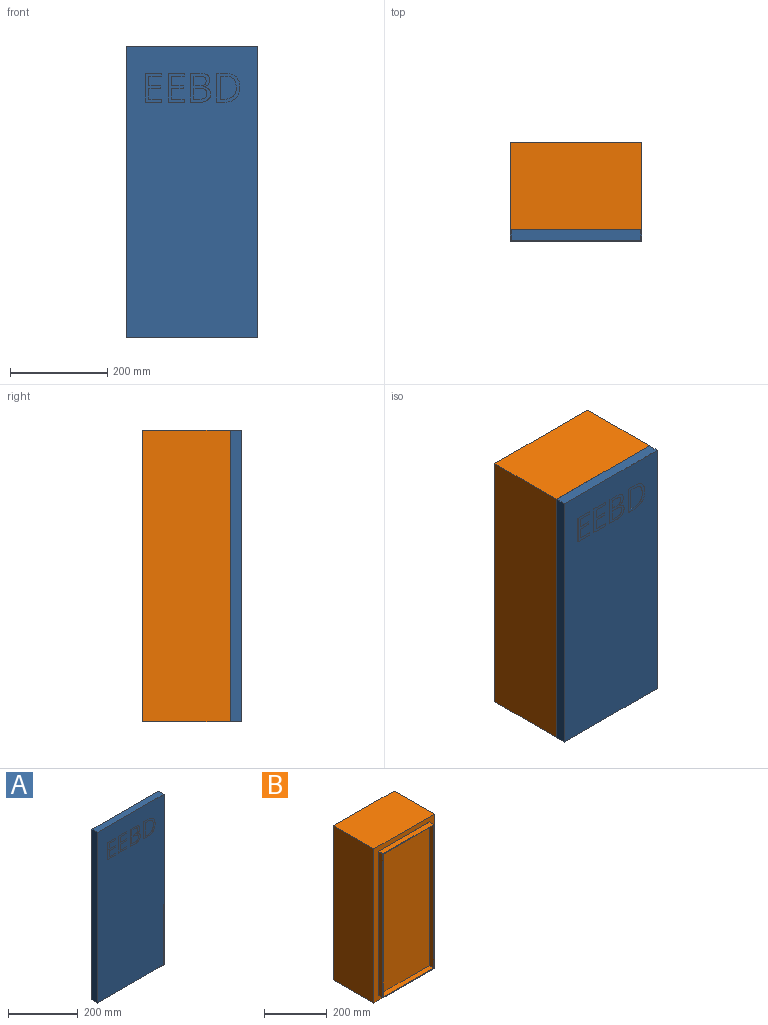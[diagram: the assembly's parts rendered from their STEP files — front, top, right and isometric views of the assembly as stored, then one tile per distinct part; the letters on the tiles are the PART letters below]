
ASSEMBLY  parts=2 mates=1
PART A: 81 faces, bbox 270x23.1x600 mm
  f0: plane 600x270mm, normal (0,-1,0), area 155520.7mm2, adj f1,f2,f3,f4,f11,f12,f13,f14
  f1: plane 600x23mm, normal (-1,0,0), area 13800mm2, adj f0,f2,f4,f5
  f2: plane 270x23mm, normal (0,0,-1), area 6210mm2, adj f0,f1,f3,f5
  f3: plane 600x23mm, normal (1,0,0), area 13800mm2, adj f0,f2,f4,f5
  f4: plane 270x23mm, normal (0,0,1), area 6210mm2, adj f0,f1,f3,f5
  f5: plane 600x270mm, normal (0,1,0), area 3464mm2, adj f1,f2,f3,f4,f6,f7,f8,f9
  f6: plane 596x21mm, normal (1,0,0), area 12516mm2, adj f5,f7,f9,f10
  f7: plane 266x21mm, normal (0,0,1), area 5586mm2, adj f5,f6,f8,f10
  f8: plane 596x21mm, normal (-1,0,0), area 12516mm2, adj f5,f7,f9,f10
  f9: plane 266x21mm, normal (0,0,-1), area 5586mm2, adj f5,f6,f8,f10
  f10: plane 596x266mm, normal (0,1,0), area 158536mm2, adj f6,f7,f8,f9
  f11: plane 6.19x0.1mm, normal (1,0,0), area 0.6mm2, adj f0,f12,f22,f23
  f12: plane 26.25x0.1mm, normal (0,0,1), area 2.6mm2, adj f0,f11,f13,f23
  f13: plane 21.89x0.1mm, normal (1,0,0), area 2.2mm2, adj f0,f12,f14,f23
  f14: plane 24.66x0.1mm, normal (0,0,-1), area 2.5mm2, adj f0,f13,f15,f23
  f15: plane 6.11x0.1mm, normal (1,0,0), area 0.6mm2, adj f0,f14,f16,f23
  f16: plane 24.66x0.1mm, normal (0,0,1), area 2.5mm2, adj f0,f15,f17,f23
  f17: plane 19.17x0.1mm, normal (1,0,0), area 1.9mm2, adj f0,f16,f18,f23
  f18: plane 26.25x0.1mm, normal (0,0,-1), area 2.6mm2, adj f0,f17,f19,f23
  f19: plane 6.15x0.1mm, normal (1,0,0), area 0.6mm2, adj f0,f18,f20,f23
  f20: plane 33.16x0.1mm, normal (0,0,1), area 3.3mm2, adj f0,f19,f21,f23
  f21: plane 59.49x0.1mm, normal (-1,0,0), area 5.9mm2, adj f0,f20,f22,f23
  f22: plane 33.16x0.1mm, normal (0,0,-1), area 3.3mm2, adj f0,f11,f21,f23
  f23: plane 59.49x33.16mm, normal (0,-1,0), area 885.6mm2, adj f11,f12,f13,f14,f15,f16,f17,f18
  f24: plane 6.19x0.1mm, normal (1,0,0), area 0.6mm2, adj f0,f25,f35,f36
  f25: plane 26.25x0.1mm, normal (0,0,1), area 2.6mm2, adj f0,f24,f26,f36
  f26: plane 21.89x0.1mm, normal (1,0,0), area 2.2mm2, adj f0,f25,f27,f36
  f27: plane 24.66x0.1mm, normal (0,0,-1), area 2.5mm2, adj f0,f26,f28,f36
  f28: plane 6.11x0.1mm, normal (1,0,0), area 0.6mm2, adj f0,f27,f29,f36
  f29: plane 24.66x0.1mm, normal (0,0,1), area 2.5mm2, adj f0,f28,f30,f36
  f30: plane 19.17x0.1mm, normal (1,0,0), area 1.9mm2, adj f0,f29,f31,f36
  f31: plane 26.25x0.1mm, normal (0,0,-1), area 2.6mm2, adj f0,f30,f32,f36
  f32: plane 6.15x0.1mm, normal (1,0,0), area 0.6mm2, adj f0,f31,f33,f36
  f33: plane 33.16x0.1mm, normal (0,0,1), area 3.3mm2, adj f0,f32,f34,f36
  f34: plane 59.49x0.1mm, normal (-1,0,0), area 5.9mm2, adj f0,f33,f35,f36
  f35: plane 33.16x0.1mm, normal (0,0,-1), area 3.3mm2, adj f0,f24,f34,f36
  f36: plane 59.49x33.16mm, normal (0,-1,0), area 885.6mm2, adj f24,f25,f26,f27,f28,f29,f30,f31
  f37: plane 59.49x0.1mm, normal (-1,0,0), area 5.9mm2, adj f0,f38,f61,f62
  f38: plane 20.76x0.1mm, normal (0,0,-1), area 2.1mm2, adj f0,f37,f39,f62
  f39: extruded ~15.08x4.48mm, area 1.6mm2, adj f0,f38,f40,f62
  f40: extruded ~12.45x5.39mm, area 1.4mm2, adj f0,f39,f41,f62
  f41: extruded ~14.24x13.55mm, area 2.2mm2, adj f0,f40,f42,f62
  f42: plane 0.4x0.1mm, normal (1,0,0), area 0mm2, adj f0,f41,f43,f62
  f43: extruded ~8.61x4.45mm, area 1mm2, adj f0,f42,f44,f62
  f44: extruded ~8.74x2.95mm, area 0.9mm2, adj f0,f43,f45,f62
  f45: extruded ~11.19x5.29mm, area 1.3mm2, adj f0,f44,f46,f62
  f46: extruded ~17.13x3.54mm, area 1.8mm2, adj f0,f45,f61,f62
  f47: plane 19.48x0.1mm, normal (1,0,0), area 1.9mm2, adj f48,f59,f62,f64
  f48: plane 10.18x0.1mm, normal (0,0,-1), area 1mm2, adj f47,f49,f62,f64
  f49: extruded ~11.39x2.21mm, area 1.2mm2, adj f48,f50,f62,f64
  f50: extruded ~7.23x3.58mm, area 0.8mm2, adj f49,f51,f62,f64
  f51: extruded ~7.74x3.22mm, area 0.9mm2, adj f50,f52,f62,f64
  f52: extruded ~10.55x2.3mm, area 1.1mm2, adj f51,f59,f62,f64
  f53: plane 11.85x0.1mm, normal (0,0,-1), area 1.2mm2, adj f54,f60,f62,f63
  f54: extruded ~11.33x2.6mm, area 1.2mm2, adj f53,f55,f62,f63
  f55: extruded ~8.14x3.72mm, area 0.9mm2, adj f54,f56,f62,f63
  f56: extruded ~8.74x3.64mm, area 1mm2, adj f55,f57,f62,f63
  f57: extruded ~10.84x2.79mm, area 1.1mm2, adj f56,f58,f62,f63
  f58: plane 12.42x0.1mm, normal (0,0,1), area 1.2mm2, adj f57,f60,f62,f63
  f59: plane 11.39x0.1mm, normal (0,0,1), area 1.1mm2, adj f47,f52,f62,f64
  f60: plane 22.27x0.1mm, normal (1,0,0), area 2.2mm2, adj f53,f58,f62,f63
  f61: plane 16.81x0.1mm, normal (0,0,1), area 1.7mm2, adj f0,f37,f46,f62
  f62: plane 59.49x41.22mm, normal (0,-1,0), area 1207mm2, adj f37,f38,f39,f40,f41,f42,f43,f44
  f63: plane 26.9x22.27mm, normal (0,-1,0), area 545.6mm2, adj f53,f54,f55,f56,f57,f58,f60
  f64: plane 25.16x19.48mm, normal (0,-1,0), area 447.8mm2, adj f47,f48,f49,f50,f51,f52,f59
  f65: extruded ~21.49x7.69mm, area 2.3mm2, adj f0,f66,f78,f79
  f66: extruded ~21.57x7.69mm, area 2.4mm2, adj f0,f65,f67,f79
  f67: plane 18.23x0.1mm, normal (0,0,1), area 1.8mm2, adj f0,f66,f68,f79
  f68: plane 59.49x0.1mm, normal (-1,0,0), area 5.9mm2, adj f0,f67,f69,f79
  f69: plane 16.48x0.1mm, normal (0,0,-1), area 1.6mm2, adj f0,f68,f70,f79
  f70: extruded ~23.01x7.79mm, area 2.5mm2, adj f0,f69,f78,f79
  f71: extruded ~18x6.23mm, area 2mm2, adj f72,f77,f79,f80
  f72: extruded ~18.6x6.09mm, area 2mm2, adj f71,f73,f79,f80
  f73: plane 8.42x0.1mm, normal (0,0,1), area 0.8mm2, adj f72,f74,f79,f80
  f74: plane 47.53x0.1mm, normal (1,0,0), area 4.8mm2, adj f73,f75,f79,f80
  f75: plane 10.05x0.1mm, normal (0,0,-1), area 1mm2, adj f74,f76,f79,f80
  f76: extruded ~17.36x5.9mm, area 1.9mm2, adj f75,f77,f79,f80
  f77: extruded ~17.54x5.84mm, area 1.9mm2, adj f71,f76,f79,f80
  f78: extruded ~22.52x7.99mm, area 2.5mm2, adj f0,f65,f70,f79
  f79: plane 59.49x47.49mm, normal (0,-1,0), area 1119.5mm2, adj f65,f66,f67,f68,f69,f70,f71,f72
  f80: plane 47.53x33.26mm, normal (0,-1,0), area 1388.2mm2, adj f71,f72,f73,f74,f75,f76,f77
PART B: 16 faces, bbox 270x200x600 mm
  f0: plane 600x270mm, normal (0,-1,0), area 33200mm2, adj f1,f2,f3,f4,f9,f10,f11,f12
  f1: plane 600x180mm, normal (-1,0,0), area 108000mm2, adj f0,f2,f4,f5
  f2: plane 270x180mm, normal (0,0,-1), area 48600mm2, adj f0,f1,f3,f5
  f3: plane 600x180mm, normal (1,0,0), area 108000mm2, adj f0,f2,f4,f5
  f4: plane 270x180mm, normal (0,0,1), area 48600mm2, adj f0,f1,f3,f5
  f5: plane 600x270mm, normal (0,1,0), area 162000mm2, adj f1,f2,f3,f4
  f6: plane 556x20mm, normal (-1,0,0), area 11120mm2, adj f7,f13,f14,f15
  f7: plane 226x20mm, normal (0,0,1), area 4520mm2, adj f6,f8,f14,f15
  f8: plane 556x20mm, normal (1,0,0), area 11120mm2, adj f7,f13,f14,f15
  f9: plane 230x20mm, normal (0,0,-1), area 4600mm2, adj f0,f10,f12,f14
  f10: plane 560x20mm, normal (1,0,0), area 11200mm2, adj f0,f9,f11,f14
  f11: plane 230x20mm, normal (0,0,1), area 4600mm2, adj f0,f10,f12,f14
  f12: plane 560x20mm, normal (-1,0,0), area 11200mm2, adj f0,f9,f11,f14
  f13: plane 226x20mm, normal (0,0,-1), area 4520mm2, adj f6,f8,f14,f15
  f14: plane 560x230mm, normal (0,-1,0), area 3144mm2, adj f6,f7,f8,f9,f10,f11,f12,f13
  f15: plane 556x226mm, normal (0,-1,0), area 125656mm2, adj f6,f7,f8,f13
PLACE A t=(-436.02,-158.03,-169.17)mm
PLACE B t=(-436.02,21.97,-169.17)mm
MATE revolute A.f4 <-> B.f4  axis (0,0,-1) through (-436.02,-158.03,430.83)mm
